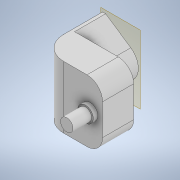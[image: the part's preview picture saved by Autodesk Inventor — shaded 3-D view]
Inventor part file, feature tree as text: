
AUTODESK INVENTOR PART (.ipt)
format: ipt  version: 2021 (Build 250183000, 183)  size: 148,992 bytes
history: native  units: mm
features: extrude x4, sketch x4, other x4, reference x3, plane x2, fillet x2, projected_geometry x1
ambient origin geometry x8: Origin, YZ Plane, XZ Plane, XY Plane, X Axis, Y Axis, Z Axis, Center Point
bodies: Solid1 (feature_tree)
feature tree (20):
  plane  "Work Plane1"
  extrude  "Extrusion1"  Depth=40.0mm
  sketch  "Sketch3"  dims[d3=40.0mm d4=20.0mm d5=0.0mm d6=15.0mm d7=10.0mm]
  plane  "Work Plane2"
  extrude  "Extrusion2"  Depth=20.0mm TaperAngle=0.0deg
  fillet  "Fillet1"  Radius=15.0mm
  fillet  "Fillet2"  Radius=10.0mm
  extrude  "Extrusion3"  Depth=10.0mm
  extrude  "Extrusion4"  Depth=3.0mm
  sketch  "Sketch2"  dims[d0=20.0mm d1=0.0mm d2=40.0mm]
  reference  "Reference2"
  reference  "Reference3"
  projected_geometry  "Projected Loop1"
  sketch  "Sketch4"  dims[d8=15.0mm d9=0.0mm d10=10.0mm]
  reference  "Reference4"
  sketch  "Sketch5"  dims[d11=3.0mm d12=0.0mm d13=0.5mm d14=0.872665mm]
  parser-record x1  (decoder bookkeeping rows leaked as tree rows — omitted from the tree; the rows remain in map.json)
  other  "ilmbt_3d_v1.iam"
  other  "knucle_MIR1:1"
  other  "base_:1"
note: 1 file-system path scrubbed to <path> (originals preserved in map.json)
